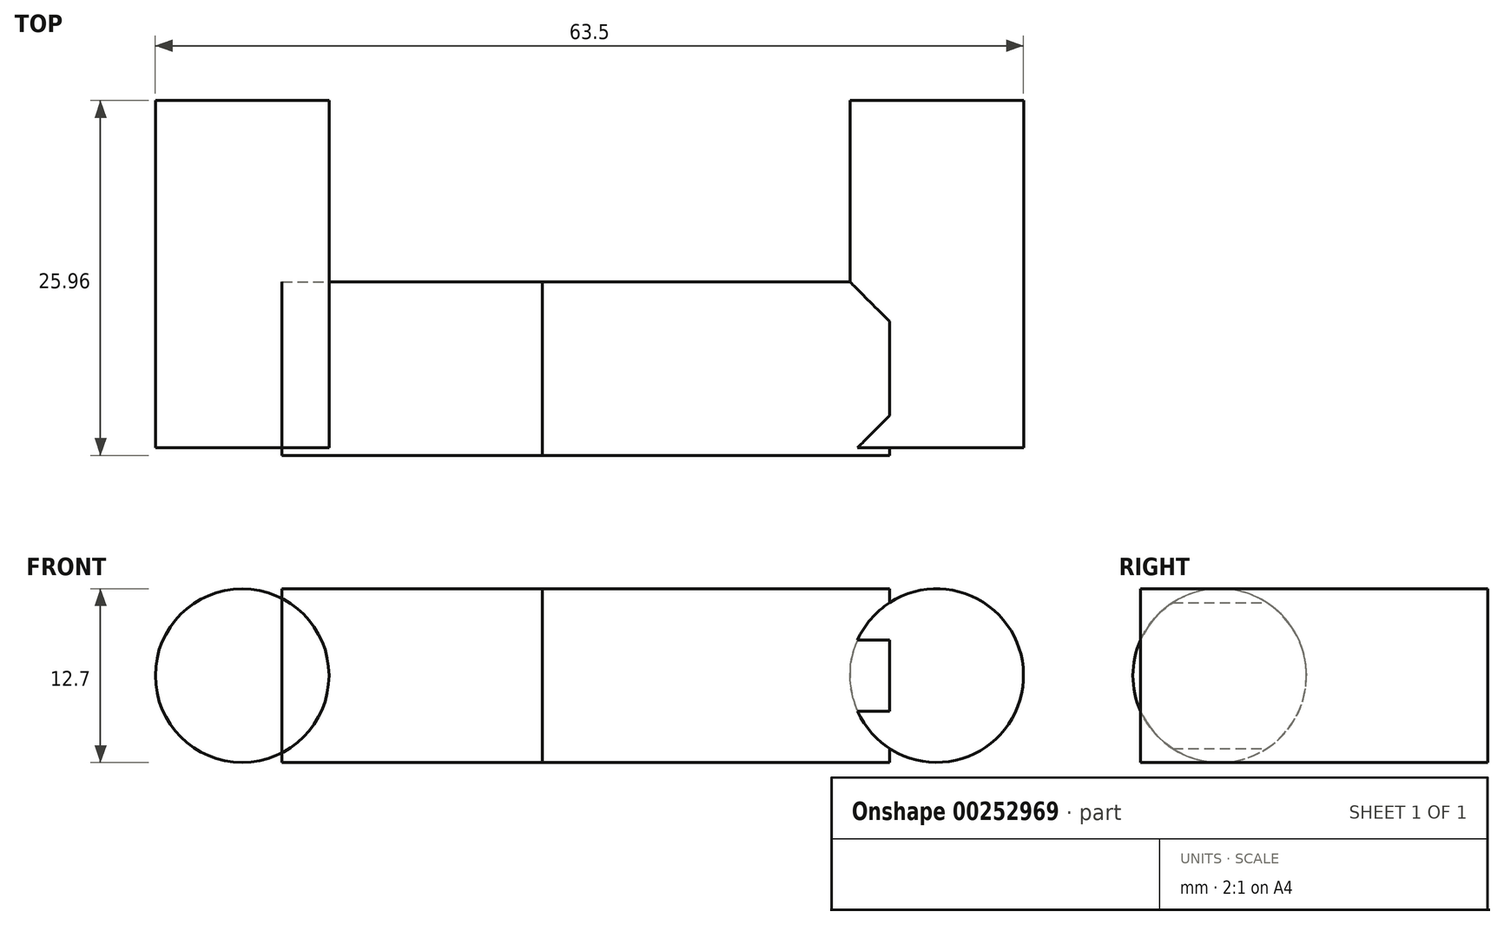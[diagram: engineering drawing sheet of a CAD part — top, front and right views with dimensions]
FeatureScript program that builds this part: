
annotation { "Feature Type Name" : "Feature", "Feature Type Description" : "" }
export const myFeature = defineFeature(function(context is Context, id is Id, definition is map)
    precondition{}
    {
        {
            var Q0;
            Q0=qCreatedBy(makeId("Front.planeOp"),FACE);
            var sketch = newSketch(context, id + "F0", { "sketchPlane" : qUnion([Q0])});
            skLineSegment(sketch, "E0", {"start": v(-21.96, 0) * mm, "end": v(28.84, 0) * mm});
            skCircle(sketch, "E1", {"center": v(-21.96, 0) * mm, "radius": 6.35 * mm});
            skCircle(sketch, "E2", {"center": v(28.84, 0) * mm, "radius": 6.35 * mm});
            skSolve(sketch);
        }
        {
            var Q0;
            Q0=makeQuery(id+"F0.imprint","IMPRINT",FACE,{"disambiguationData":[TD([[makeQuery(id+"F0.imprint","IMPRINT",EDGE,{"derivedFrom":sQuery(id+"F0.wireOp",EDGE,"E1")}),1.0]])]});
            var Q1;
            Q1=makeQuery(id+"F0.imprint","IMPRINT",FACE,{"disambiguationData":[TD([[makeQuery(id+"F0.imprint","IMPRINT",EDGE,{"derivedFrom":sQuery(id+"F0.wireOp",EDGE,"E2")}),1.0]])]});
            extrude(context, id + "F1", {"entities" : qUnion([Q0, Q1]), "depth" : 25.4 * mm});
        }
        {
            var Q0;
            Q0=qCreatedBy(makeId("Right.planeOp"),FACE);
            var sketch = newSketch(context, id + "F2", { "sketchPlane" : qUnion([Q0])});
            skCircle(sketch, "E3", {"center": v(-19.6, 0) * mm, "radius": 6.35 * mm});
            skSolve(sketch);
        }
        {
            var Q0;
            Q0=makeQuery(id+"F2.imprint","IMPRINT",FACE,{"disambiguationData":[TD([[makeQuery(id+"F2.imprint","IMPRINT",EDGE,{"derivedFrom":sQuery(id+"F2.wireOp",EDGE,"E3")}),1.0]])]});
            extrude(context, id + "F3", {"entities" : qUnion([Q0]), "operationType" : NewBodyOperationType.ADD, "depth" : 25.4 * mm});
        }
        {
            var Q0;
            Q0 = qSketchRegion(id + "F2", true);
            extrude(context, id + "F4", {"entities" : qUnion([Q0]), "oppositeDirection" : true, "depth" : 19.05 * mm});
        }
    });
